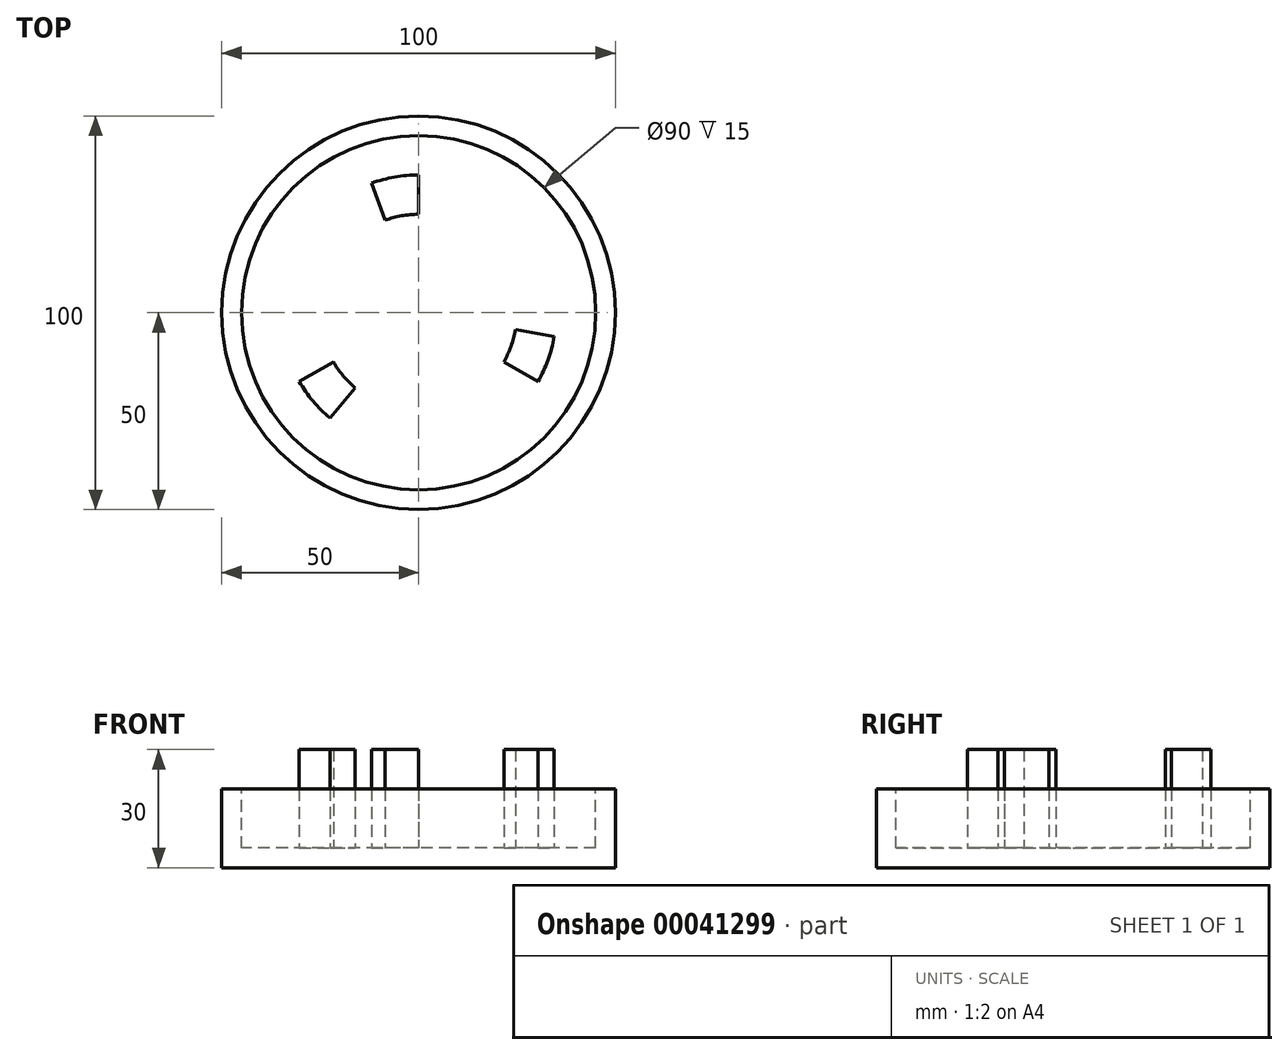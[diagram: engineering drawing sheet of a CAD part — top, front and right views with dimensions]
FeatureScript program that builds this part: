
annotation { "Feature Type Name" : "Feature", "Feature Type Description" : "" }
export const myFeature = defineFeature(function(context is Context, id is Id, definition is map)
    precondition{}
    {
        {
            var Q0;
            Q0=qCreatedBy(makeId("Top.planeOp"),FACE);
            var sketch = newSketch(context, id + "F0", { "sketchPlane" : qUnion([Q0])});
            skCircle(sketch, "E0", {"center": v(0, 0) * mm, "radius": 50 * mm});
            skSolve(sketch);
        }
        {
            var Q0;
            Q0=makeQuery(id+"F0.imprint","IMPRINT",FACE,{"disambiguationData":[TD([[makeQuery(id+"F0.imprint","IMPRINT",EDGE,{"derivedFrom":sQuery(id+"F0.wireOp",EDGE,"E0")}),1.0]])]});
            extrude(context, id + "F1", {"entities" : qUnion([Q0]), "depth" : 20 * mm});
        }
        {
            var Q0;
            Q0=makeQuery(id+"F1.opExtrude","CAP_FACE",FACE,{"disambiguationData":[OSD([sQuery(id+"F0.wireOp",EDGE,"E0")])],"isStart":false});
            var sketch = newSketch(context, id + "F2", { "sketchPlane" : qUnion([Q0])});
            skCircle(sketch, "E1", {"center": v(0, 0) * mm, "radius": 45 * mm});
            skSolve(sketch);
        }
        {
            var Q0;
            Q0 = qSketchRegion(id + "F2", true);
            extrude(context, id + "F3", {"entities" : qUnion([Q0]), "operationType" : NewBodyOperationType.REMOVE, "oppositeDirection" : true, "depth" : 15 * mm});
        }
        {
            var Q0;
            Q0=makeQuery(id+"F3.boolean.opBoolean","COPY",FACE,{"derivedFrom":makeQuery(id+"F3.opExtrude","CAP_FACE",FACE,{"disambiguationData":[OSD([sQuery(id+"F2.wireOp",EDGE,"E1")])],"isStart":false})});
            var sketch = newSketch(context, id + "F4", { "sketchPlane" : qUnion([Q0])});
            skCircle(sketch, "E2", {"center": v(0, 0) * mm, "radius": 15 * mm, "construction": true});
            skCircle(sketch, "E3", {"center": v(0, 0) * mm, "radius": 25 * mm, "construction": true});
            skCircle(sketch, "E4", {"center": v(0, 0) * mm, "radius": 35 * mm, "construction": true});
            skCircle(sketch, "E5", {"center": v(0, 0) * mm, "radius": 5 * mm, "construction": true});
            skLineSegment(sketch, "E6", {"start": v(0, 0) * mm, "end": v(-23.21, 63.77) * mm, "construction": true});
            skLineSegment(sketch, "E7", {"start": v(0, 0) * mm, "end": v(0, 65.86) * mm, "construction": true});
            skArc(sketch, "E8", {"start": v(-11.97, 32.89) * mm, "mid": v(-6.08, 34.47) * mm, "end": v(0, 35) * mm});
            skArc(sketch, "E9", {"start": v(-8.55, 23.5) * mm, "mid": v(-4.34, 24.62) * mm, "end": v(0, 25) * mm});
            skLineSegment(sketch, "E10", {"start": v(-11.97, 32.89) * mm, "end": v(-8.55, 23.5) * mm});
            skLineSegment(sketch, "E11", {"start": v(0, 35) * mm, "end": v(0, 25) * mm});
            skArc(sketch, "E12.1.0", {"start": v(-22.5, -26.81) * mm, "mid": v(-26.81, -22.5) * mm, "end": v(-30.31, -17.5) * mm});
            skLineSegment(sketch, "E12.1.1", {"start": v(-22.5, -26.81) * mm, "end": v(-16.07, -19.15) * mm});
            skArc(sketch, "E12.1.2", {"start": v(-16.07, -19.15) * mm, "mid": v(-19.15, -16.07) * mm, "end": v(-21.65, -12.5) * mm});
            skLineSegment(sketch, "E12.1.3", {"start": v(-30.31, -17.5) * mm, "end": v(-21.65, -12.5) * mm});
            skArc(sketch, "E12.2.0", {"start": v(34.47, -6.08) * mm, "mid": v(32.89, -11.97) * mm, "end": v(30.31, -17.5) * mm});
            skLineSegment(sketch, "E12.2.1", {"start": v(34.47, -6.08) * mm, "end": v(24.62, -4.34) * mm});
            skArc(sketch, "E12.2.2", {"start": v(24.62, -4.34) * mm, "mid": v(23.5, -8.55) * mm, "end": v(21.65, -12.5) * mm});
            skLineSegment(sketch, "E12.2.3", {"start": v(30.31, -17.5) * mm, "end": v(21.65, -12.5) * mm});
            skSolve(sketch);
        }
        {
            var Q0;
            Q0 = qSketchRegion(id + "F4", true);
            extrude(context, id + "F5", {"entities" : qUnion([Q0]), "operationType" : NewBodyOperationType.ADD, "depth" : 25 * mm});
        }
    });
